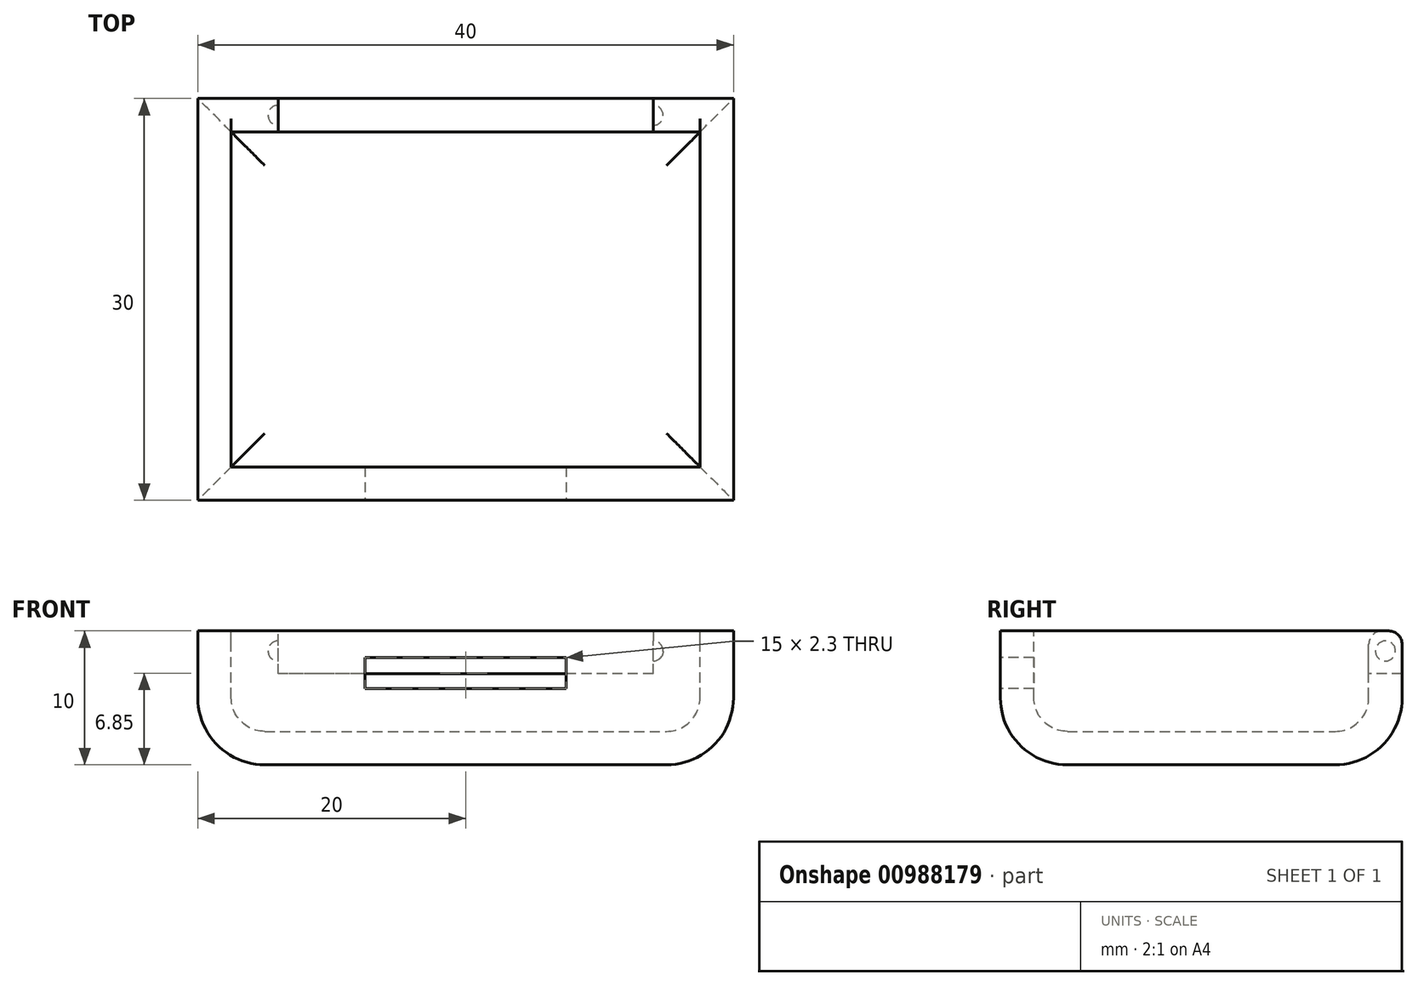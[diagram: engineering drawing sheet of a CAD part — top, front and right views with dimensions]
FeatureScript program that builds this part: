
annotation { "Feature Type Name" : "Feature", "Feature Type Description" : "" }
export const myFeature = defineFeature(function(context is Context, id is Id, definition is map)
    precondition{}
    {
        {
            var Q0;
            Q0=qCreatedBy(makeId("Top.planeOp"),FACE);
            var sketch = newSketch(context, id + "F0", { "sketchPlane" : qUnion([Q0])});
            skLineSegment(sketch, "E0.bottom", {"start": v(20, 15) * mm, "end": v(-20, 15) * mm});
            skLineSegment(sketch, "E0.top", {"start": v(20, -15) * mm, "end": v(-20, -15) * mm});
            skLineSegment(sketch, "E0.left", {"start": v(20, 15) * mm, "end": v(20, -15) * mm});
            skLineSegment(sketch, "E0.right", {"start": v(-20, 15) * mm, "end": v(-20, -15) * mm});
            skPoint(sketch, "E0.middle", {"position": v(0, 0) * mm});
            skSolve(sketch);
        }
        {
            var Q0;
            Q0 = qSketchRegion(id + "F0", true);
            extrude(context, id + "F1", {"entities" : qUnion([Q0]), "oppositeDirection" : true, "depth" : 10 * mm, "offsetDistance" : 25 * mm});
        }
        {
            var Q0;
            Q0=makeQuery(id+"F1.opExtrude","CAP_FACE",FACE,{"disambiguationData":[OSD([sQuery(id+"F0.wireOp",EDGE,"E0.bottom"),sQuery(id+"F0.wireOp",EDGE,"E0.top"),sQuery(id+"F0.wireOp",EDGE,"E0.left"),sQuery(id+"F0.wireOp",EDGE,"E0.right")])],"isStart":false});
            fillet(context, id + "F2", {"entities" : qUnion([Q0]), "radius" : 5 * mm, "tangentPropagation" : true, "allowEdgeOverflow" : false});
        }
        {
            var Q0;
            Q0=makeQuery(id+"F1.opExtrude","CAP_FACE",FACE,{"disambiguationData":[OSD([sQuery(id+"F0.wireOp",EDGE,"E0.bottom"),sQuery(id+"F0.wireOp",EDGE,"E0.top"),sQuery(id+"F0.wireOp",EDGE,"E0.left"),sQuery(id+"F0.wireOp",EDGE,"E0.right")])],"isStart":true});
            shell(context, id + "F3", {"entities" : qUnion([Q0]), "thickness" : 2.5 * mm});
        }
        {
            var Q0;
            Q0=makeQuery(id+"F1.opExtrude","CAP_FACE",FACE,{"disambiguationData":[OSD([sQuery(id+"F0.wireOp",EDGE,"E0.bottom"),sQuery(id+"F0.wireOp",EDGE,"E0.top"),sQuery(id+"F0.wireOp",EDGE,"E0.left"),sQuery(id+"F0.wireOp",EDGE,"E0.right")])],"isStart":true});
            var sketch = newSketch(context, id + "F4", { "sketchPlane" : qUnion([Q0])});
            skLineSegment(sketch, "E1.bottom", {"start": v(-14, 15) * mm, "end": v(14, 15) * mm});
            skLineSegment(sketch, "E1.top", {"start": v(-14, 12.5) * mm, "end": v(14, 12.5) * mm});
            skLineSegment(sketch, "E1.left", {"start": v(-14, 15) * mm, "end": v(-14, 12.5) * mm});
            skLineSegment(sketch, "E1.right", {"start": v(14, 15) * mm, "end": v(14, 12.5) * mm});
            skPoint(sketch, "E2", {"position": v(0, 15) * mm});
            skSolve(sketch);
        }
        {
            var Q0;
            Q0 = qSketchRegion(id + "F4", true);
            extrude(context, id + "F5", {"entities" : qUnion([Q0]), "operationType" : NewBodyOperationType.REMOVE, "oppositeDirection" : true, "depth" : 3 * mm, "offsetDistance" : 25 * mm});
        }
        {
            var Q0;
            Q0=qCreatedBy(makeId("Top.planeOp"),FACE);
            var sketch = newSketch(context, id + "F6", { "sketchPlane" : qUnion([Q0])});
            skLineSegment(sketch, "E3.bottom", {"start": v(0, 28.07) * mm, "end": v(32.36, 28.07) * mm});
            skLineSegment(sketch, "E3.top", {"start": v(0, -32.18) * mm, "end": v(32.36, -32.18) * mm});
            skLineSegment(sketch, "E3.left", {"start": v(0, 28.07) * mm, "end": v(0, -32.18) * mm});
            skLineSegment(sketch, "E3.right", {"start": v(32.36, 28.07) * mm, "end": v(32.36, -32.18) * mm});
            skSolve(sketch);
        }
        {
            var Q0;
            Q0 = qSketchRegion(id + "F6", true);
            extrude(context, id + "F7", {"entities" : qUnion([Q0]), "operationType" : NewBodyOperationType.REMOVE, "oppositeDirection" : true, "depth" : 25 * mm, "offsetDistance" : 25 * mm});
        }
        {
            var Q0;
            Q0=makeQuery(id+"F5.boolean.opBoolean","COPY",FACE,{"derivedFrom":makeQuery(id+"F5.opExtrude","SWEPT_FACE",FACE,{"disambiguationData":[OSD([sQuery(id+"F4.wireOp",EDGE,"E1.left")])]})});
            var sketch = newSketch(context, id + "F8", { "sketchPlane" : qUnion([Q0])});
            skCircle(sketch, "E4", {"center": v(13.75, -1.5) * mm, "radius": 0.75 * mm});
            skPoint(sketch, "E5", {"position": v(13.75, 0) * mm});
            skPoint(sketch, "E6", {"position": v(15, -1.5) * mm});
            skSolve(sketch);
        }
        {
            var Q0;
            Q0=makeQuery(id+"F8.imprint","IMPRINT",FACE,{"disambiguationData":[TD([[makeQuery(id+"F8.imprint","IMPRINT",EDGE,{"derivedFrom":sQuery(id+"F8.wireOp",EDGE,"E4")}),1.0]])]});
            var Q1;
            Q1=sQuery(id+"F8.wireOp",EDGE,"E4");
            extrude(context, id + "F9", {"entities" : qUnion([Q0]), "operationType" : NewBodyOperationType.REMOVE, "surfaceEntities" : qUnion([Q1]), "oppositeDirection" : true, "depth" : .75 * mm, "offsetDistance" : 25 * mm});
        }
        {
            var Q0;
            Q0=makeQuery(id+"F9.boolean.opBoolean","COPY",EDGE,{"derivedFrom":makeQuery(id+"F9.opExtrude","CAP_EDGE",EDGE,{"disambiguationData":[OSD([sQuery(id+"F8.wireOp",EDGE,"E4")])],"isStart":false})});
            fillet(context, id + "F10", {"entities" : qUnion([Q0]), "radius" : .75 * mm, "tangentPropagation" : true, "allowEdgeOverflow" : false});
        }
        {
            var Q0;
            Q0=makeQuery(id+"F5.boolean.opBoolean","COPY",FACE,{"derivedFrom":makeQuery(id+"F5.opExtrude","CAP_FACE",FACE,{"disambiguationData":[OSD([sQuery(id+"F4.wireOp",EDGE,"E1.bottom"),sQuery(id+"F4.wireOp",EDGE,"E1.top"),sQuery(id+"F4.wireOp",EDGE,"E1.left"),sQuery(id+"F4.wireOp",EDGE,"E1.right")])],"isStart":false})});
            var sketch = newSketch(context, id + "F11", { "sketchPlane" : qUnion([Q0])});
            skLineSegment(sketch, "E7.0.0", {"start": v(0, 12.5) * mm, "end": v(0, 15) * mm});
            skLineSegment(sketch, "E7.0.1", {"start": v(0, 15) * mm, "end": v(-14, 15) * mm});
            skLineSegment(sketch, "E7.0.2", {"start": v(-14, 15) * mm, "end": v(-14, 12.5) * mm});
            skLineSegment(sketch, "E7.0.3", {"start": v(-14, 12.5) * mm, "end": v(0, 12.5) * mm});
            skSolve(sketch);
        }
        {
            var Q0;
            Q0 = qSketchRegion(id + "F11", true);
            extrude(context, id + "F12", {"entities" : qUnion([Q0]), "operationType" : NewBodyOperationType.REMOVE, "oppositeDirection" : true, "depth" : .2 * mm, "offsetDistance" : 25 * mm});
        }
        {
            var Q0;
            {var subQ0=sQuery(id+"F0.wireOp",EDGE,"E0.bottom");var subQ1=sQuery(id+"F0.wireOp",EDGE,"E0.right");Q0=makeQuery(id+"F5.boolean.opBoolean","SPLIT",EDGE,{"disambiguationData":[TD([makeQuery(id+"F1.opExtrude","SWEPT_FACE",FACE,{"disambiguationData":[OSD([subQ1])]})])],"derivedFrom":makeQuery(id+"F1.opExtrude","CAP_EDGE",EDGE,{"disambiguationData":[OSD([subQ0])],"isStart":true})});}
            var Q1;
            {var subQ1=sQuery(id+"F0.wireOp",EDGE,"E0.bottom");Q1=makeQuery(id+"F5.boolean.opBoolean","SPLIT",EDGE,{"disambiguationData":[TD([makeQuery(id+"F5.opExtrude","SWEPT_FACE",FACE,{"disambiguationData":[OSD([sQuery(id+"F4.wireOp",EDGE,"E1.left")])]})])],"derivedFrom":makeQuery(id+"F3.opShell","OFFSET_EDGE",EDGE,{"disambiguationData":[OSD([subQ1]),TDD([makeQuery(id+"F1.opExtrude","CAP_EDGE",EDGE,{"disambiguationData":[OSD([subQ1])],"isStart":true})])]})});}
            var Q2;
            Q2=makeQuery(id+"F12.boolean.opBoolean","COPY",EDGE,{"derivedFrom":makeQuery(id+"F12.opExtrude","CAP_EDGE",EDGE,{"disambiguationData":[OSD([sQuery(id+"F11.wireOp",EDGE,"E7.0.1")])],"isStart":false})});
            var Q3;
            Q3=makeQuery(id+"F12.boolean.opBoolean","COPY",EDGE,{"derivedFrom":makeQuery(id+"F12.opExtrude","CAP_EDGE",EDGE,{"disambiguationData":[OSD([sQuery(id+"F11.wireOp",EDGE,"E7.0.3")])],"isStart":false})});
            fillet(context, id + "F13", {"entities" : qUnion([Q0, Q1, Q2, Q3]), "radius" : 1 * mm, "tangentPropagation" : true, "allowEdgeOverflow" : false});
        }
        {
            var Q0;
            Q0=makeQuery(id+"F1.opExtrude","SWEPT_BODY",BODY,{"disambiguationData":[OSD([sQuery(id+"F0.wireOp",EDGE,"E0.bottom"),sQuery(id+"F0.wireOp",EDGE,"E0.top"),sQuery(id+"F0.wireOp",EDGE,"E0.left"),sQuery(id+"F0.wireOp",EDGE,"E0.right")])]});
            var Q1;
            Q1=qCreatedBy(makeId("Right.planeOp"),FACE);
            mirror(context, id + "F14", {"operationType" : NewBodyOperationType.ADD, "entities" : qUnion([Q0]), "mirrorPlane" : qUnion([Q1])});
        }
        {
            var Q0;
            {var subQ0=makeQuery(id+"F1.opExtrude","SWEPT_FACE",FACE,{"disambiguationData":[OSD([sQuery(id+"F0.wireOp",EDGE,"E0.top")])]});Q0=makeQuery(id+"F14.boolean.opBoolean","MERGE",FACE,{"derivedFrom":[subQ0,makeQuery(id+"F14.opPattern","COPY",FACE,{"derivedFrom":subQ0,"instanceName":"1"})]});}
            var sketch = newSketch(context, id + "F15", { "sketchPlane" : qUnion([Q0])});
            skLineSegment(sketch, "E8.bottom", {"start": v(7.5, -2) * mm, "end": v(-7.5, -2) * mm});
            skLineSegment(sketch, "E8.top", {"start": v(7.5, -4.3) * mm, "end": v(-7.5, -4.3) * mm});
            skLineSegment(sketch, "E8.left", {"start": v(7.5, -2) * mm, "end": v(7.5, -4.3) * mm});
            skLineSegment(sketch, "E8.right", {"start": v(-7.5, -2) * mm, "end": v(-7.5, -4.3) * mm});
            skPoint(sketch, "E8.middle", {"position": v(0, -3.15) * mm});
            skSolve(sketch);
        }
        {
            var Q0;
            Q0 = qSketchRegion(id + "F15", true);
            extrude(context, id + "F16", {"entities" : qUnion([Q0]), "operationType" : NewBodyOperationType.REMOVE, "endBound" : BoundingType.UP_TO_NEXT, "oppositeDirection" : true, "depth" : 25 * mm, "offsetDistance" : 25 * mm});
        }
    });
